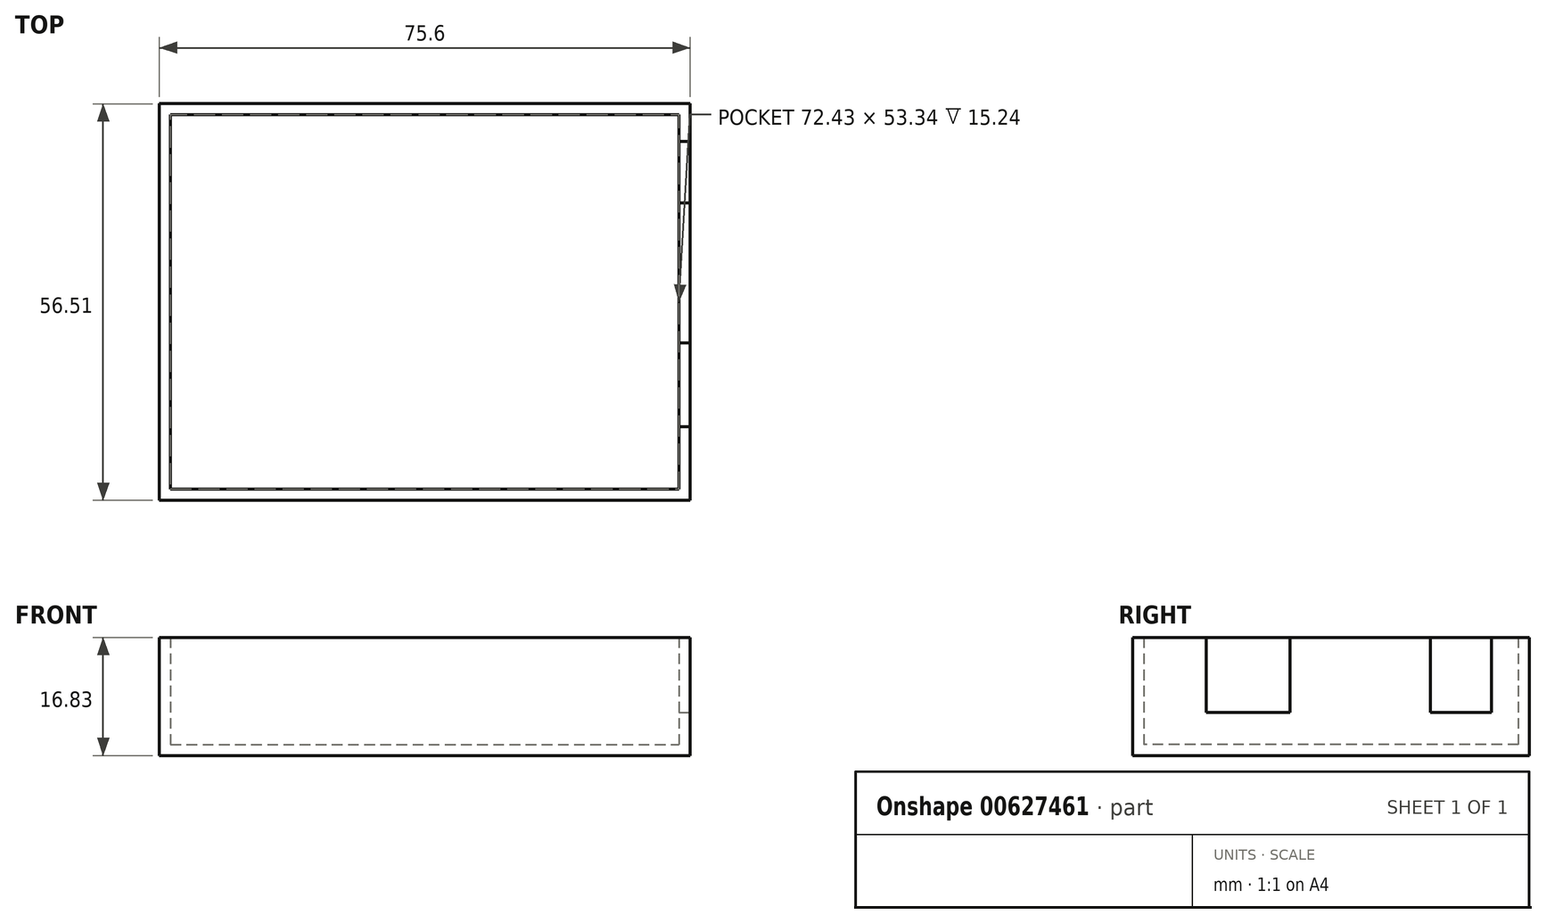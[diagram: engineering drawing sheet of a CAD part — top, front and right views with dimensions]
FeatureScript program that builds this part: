
annotation { "Feature Type Name" : "Feature", "Feature Type Description" : "" }
export const myFeature = defineFeature(function(context is Context, id is Id, definition is map)
    precondition{}
    {
        {
            var Q0;
            Q0=qCreatedBy(makeId("Top.planeOp"),FACE);
            var sketch = newSketch(context, id + "F0", { "sketchPlane" : qUnion([Q0])});
            skLineSegment(sketch, "E0.bottom", {"start": v(-21.87, 29.31) * mm, "end": v(53.73, 29.31) * mm});
            skLineSegment(sketch, "E0.top", {"start": v(-21.87, -27.2) * mm, "end": v(53.73, -27.2) * mm});
            skLineSegment(sketch, "E0.left", {"start": v(-21.87, 29.31) * mm, "end": v(-21.87, -27.2) * mm});
            skLineSegment(sketch, "E0.right", {"start": v(53.73, 29.31) * mm, "end": v(53.73, -27.2) * mm});
            skSolve(sketch);
        }
        {
            var Q0;
            Q0 = qSketchRegion(id + "F0", true);
            extrude(context, id + "F1", {"entities" : qUnion([Q0]), "depth" : 16.83 * mm, "offsetDistance" : 25.4 * mm});
        }
        {
            var Q0;
            Q0=makeQuery(id+"F1.opExtrude","CAP_FACE",FACE,{"disambiguationData":[OSD([sQuery(id+"F0.wireOp",EDGE,"E0.bottom"),sQuery(id+"F0.wireOp",EDGE,"E0.top"),sQuery(id+"F0.wireOp",EDGE,"E0.left"),sQuery(id+"F0.wireOp",EDGE,"E0.right")])],"isStart":false});
            shell(context, id + "F2", {"entities" : qUnion([Q0]), "thickness" : 1.59 * mm});
        }
        {
            var Q0;
            Q0=makeQuery(id+"F1.opExtrude","SWEPT_FACE",FACE,{"disambiguationData":[OSD([sQuery(id+"F0.wireOp",EDGE,"E0.right")])]});
            var sketch = newSketch(context, id + "F3", { "sketchPlane" : qUnion([Q0])});
            skLineSegment(sketch, "E1.bottom", {"start": v(-16.72, 16.83) * mm, "end": v(-4.79, 16.83) * mm});
            skLineSegment(sketch, "E1.top", {"start": v(-16.72, 6.16) * mm, "end": v(-4.79, 6.16) * mm});
            skLineSegment(sketch, "E1.left", {"start": v(-16.72, 16.83) * mm, "end": v(-16.72, 6.16) * mm});
            skLineSegment(sketch, "E1.right", {"start": v(-4.79, 16.83) * mm, "end": v(-4.79, 6.16) * mm});
            skLineSegment(sketch, "E2.bottom", {"start": v(23.93, 16.83) * mm, "end": v(15.2, 16.83) * mm});
            skLineSegment(sketch, "E2.top", {"start": v(23.93, 6.16) * mm, "end": v(15.2, 6.16) * mm});
            skLineSegment(sketch, "E2.left", {"start": v(23.93, 16.83) * mm, "end": v(23.93, 6.16) * mm});
            skLineSegment(sketch, "E2.right", {"start": v(15.2, 16.83) * mm, "end": v(15.2, 6.16) * mm});
            skSolve(sketch);
        }
        {
            var Q0;
            Q0 = qSketchRegion(id + "F3", true);
            extrude(context, id + "F4", {"entities" : qUnion([Q0]), "operationType" : NewBodyOperationType.REMOVE, "oppositeDirection" : true, "depth" : 1.59 * mm, "offsetDistance" : 25.4 * mm});
        }
    });
